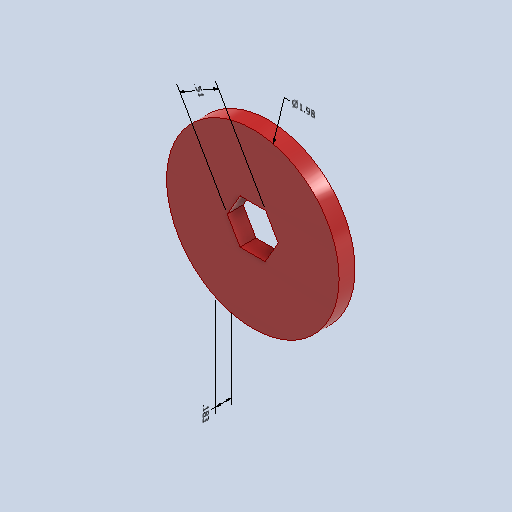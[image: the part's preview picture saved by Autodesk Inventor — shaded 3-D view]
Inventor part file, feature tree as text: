
AUTODESK INVENTOR PART (.ipt)
format: ipt  version: 2022.1 (Build 261234000, 234)  size: 134,656 bytes
history: native  units: in
note: dims shown in document units (in); Inventor stores cm internally (conversion verified against a paired STEP export)
features: other x5, extrude x1, thicken_offset x1, sketch x1
ambient origin geometry x8: Origin, YZ Plane, XZ Plane, XY Plane, X Axis, Y Axis, Z Axis, Center Point
bodies: Solid1 (feature_tree)
feature tree (8):
  other  "Annotations"
  extrude  "Extrusion1"  Depth=0.1825in
  other  "Reduce Outside Diameter"
  thicken_offset  "Thicken2"
  sketch  "Sketch1"  dims[d0=0.5in d2=1.99in d3=0.7063in d4=0.1875in d5=0.0in d6=0.005in d7=0.005in d8=0.005in d9=0.005in d10=0.5245in d11=1.98in d12=0.1538in d13=0.51in d14=0.1112in d15=0.3058in d16=0.1825in]
  other  "Diameter Dimension 1"
  other  "Linear Dimension 1"
  other  "Linear Dimension 2"
